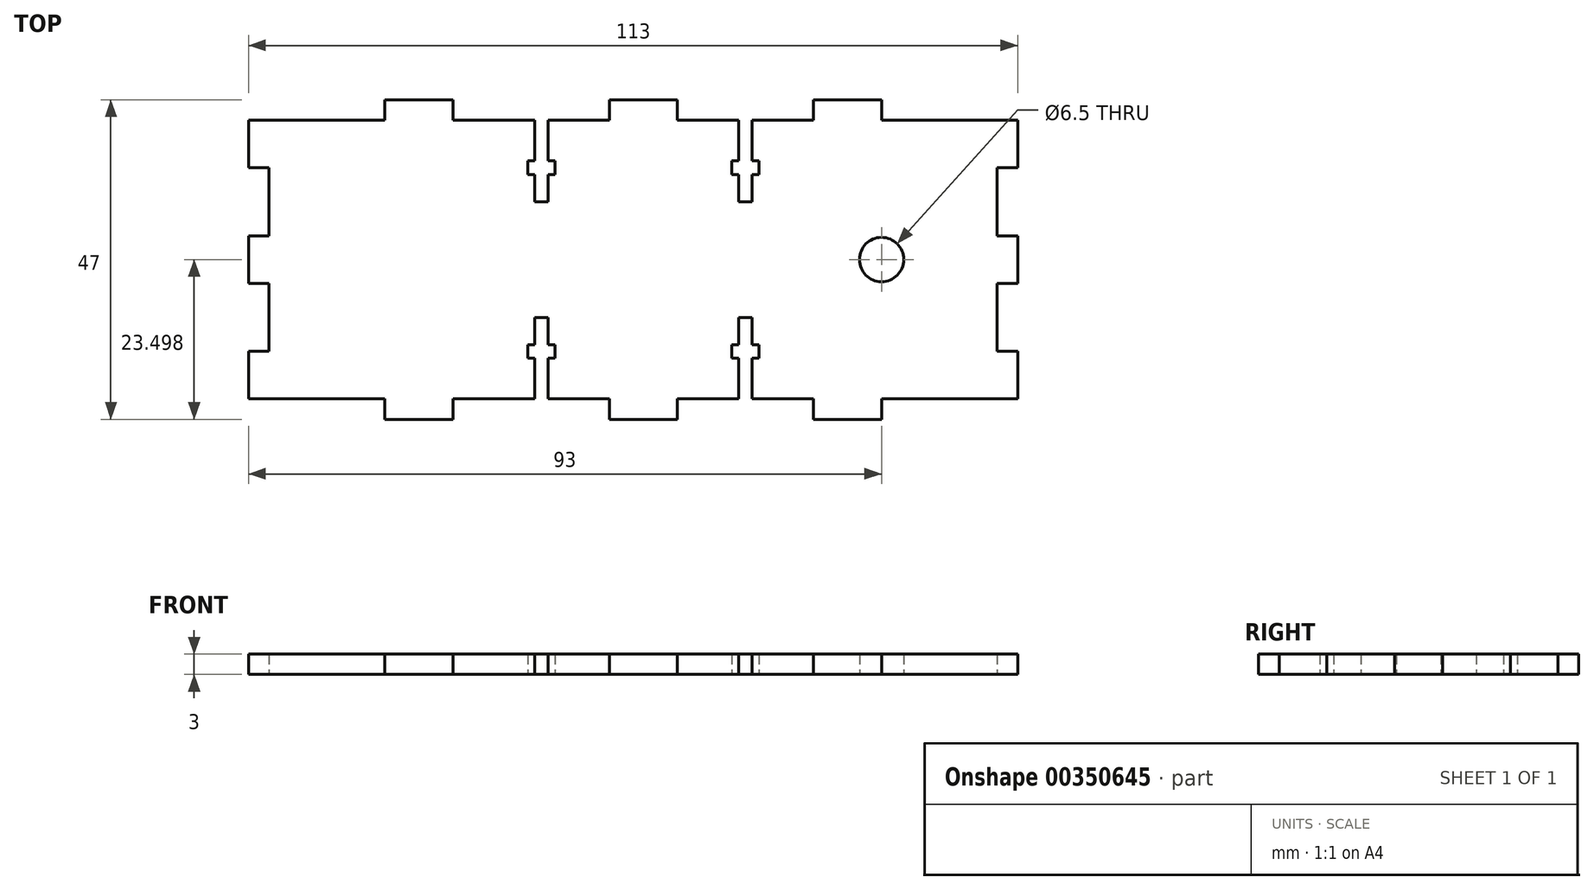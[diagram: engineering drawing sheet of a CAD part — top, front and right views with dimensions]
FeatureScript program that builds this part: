
annotation { "Feature Type Name" : "Feature", "Feature Type Description" : "" }
export const myFeature = defineFeature(function(context is Context, id is Id, definition is map)
    precondition{}
    {
        {
            var Q0;
            Q0=qCreatedBy(makeId("Top.planeOp"),FACE);
            var sketch = newSketch(context, id + "F0", { "sketchPlane" : qUnion([Q0])});
            skLineSegment(sketch, "E0", {"start": v(55.08, -54.23) * mm, "end": v(55.08, -47.23) * mm});
            skLineSegment(sketch, "E1", {"start": v(55.08, -47.23) * mm, "end": v(52.08, -47.23) * mm});
            skLineSegment(sketch, "E2", {"start": v(52.08, -47.23) * mm, "end": v(52.08, -37.23) * mm});
            skLineSegment(sketch, "E3", {"start": v(52.08, -37.23) * mm, "end": v(55.08, -37.23) * mm});
            skLineSegment(sketch, "E4", {"start": v(55.08, -37.23) * mm, "end": v(55.08, -30.23) * mm});
            skLineSegment(sketch, "E5", {"start": v(55.08, -30.23) * mm, "end": v(52.08, -30.23) * mm});
            skLineSegment(sketch, "E6", {"start": v(52.08, -30.23) * mm, "end": v(52.08, -20.23) * mm});
            skLineSegment(sketch, "E7", {"start": v(52.08, -20.23) * mm, "end": v(55.08, -20.23) * mm});
            skLineSegment(sketch, "E8", {"start": v(55.08, -20.23) * mm, "end": v(55.08, -13.23) * mm});
            skLineSegment(sketch, "E9", {"start": v(55.08, -13.23) * mm, "end": v(35.08, -13.23) * mm});
            skLineSegment(sketch, "E10", {"start": v(35.08, -13.23) * mm, "end": v(35.08, -10.23) * mm});
            skLineSegment(sketch, "E11", {"start": v(35.08, -10.23) * mm, "end": v(25.08, -10.23) * mm});
            skLineSegment(sketch, "E12", {"start": v(25.08, -10.23) * mm, "end": v(25.08, -13.23) * mm});
            skLineSegment(sketch, "E13", {"start": v(5.08, -13.23) * mm, "end": v(5.08, -10.23) * mm});
            skLineSegment(sketch, "E14", {"start": v(5.08, -10.23) * mm, "end": v(-4.92, -10.23) * mm});
            skLineSegment(sketch, "E15", {"start": v(-4.92, -10.23) * mm, "end": v(-4.92, -13.23) * mm});
            skLineSegment(sketch, "E16", {"start": v(-27.92, -13.23) * mm, "end": v(-27.92, -10.23) * mm});
            skLineSegment(sketch, "E17", {"start": v(-27.92, -10.23) * mm, "end": v(-37.92, -10.23) * mm});
            skLineSegment(sketch, "E18", {"start": v(-37.92, -10.23) * mm, "end": v(-37.92, -13.23) * mm});
            skLineSegment(sketch, "E19", {"start": v(-37.92, -13.23) * mm, "end": v(-57.92, -13.23) * mm});
            skLineSegment(sketch, "E20", {"start": v(-57.92, -13.23) * mm, "end": v(-57.92, -20.23) * mm});
            skLineSegment(sketch, "E21", {"start": v(-57.92, -20.23) * mm, "end": v(-54.92, -20.23) * mm});
            skLineSegment(sketch, "E22", {"start": v(-54.92, -20.23) * mm, "end": v(-54.92, -30.23) * mm});
            skLineSegment(sketch, "E23", {"start": v(-54.92, -30.23) * mm, "end": v(-57.92, -30.23) * mm});
            skLineSegment(sketch, "E24", {"start": v(-57.92, -30.23) * mm, "end": v(-57.92, -37.23) * mm});
            skLineSegment(sketch, "E25", {"start": v(-57.92, -37.23) * mm, "end": v(-54.92, -37.23) * mm});
            skLineSegment(sketch, "E26", {"start": v(-54.92, -37.23) * mm, "end": v(-54.92, -47.23) * mm});
            skLineSegment(sketch, "E27", {"start": v(-54.92, -47.23) * mm, "end": v(-57.92, -47.23) * mm});
            skLineSegment(sketch, "E28", {"start": v(-57.92, -54.23) * mm, "end": v(-37.92, -54.23) * mm});
            skLineSegment(sketch, "E29", {"start": v(-37.92, -54.23) * mm, "end": v(-37.92, -57.23) * mm});
            skLineSegment(sketch, "E30", {"start": v(-37.92, -57.23) * mm, "end": v(-27.92, -57.23) * mm});
            skLineSegment(sketch, "E31", {"start": v(-27.92, -57.23) * mm, "end": v(-27.92, -54.23) * mm});
            skLineSegment(sketch, "E32", {"start": v(-4.92, -54.23) * mm, "end": v(-4.92, -57.23) * mm});
            skLineSegment(sketch, "E33", {"start": v(-4.92, -57.23) * mm, "end": v(5.08, -57.23) * mm});
            skLineSegment(sketch, "E34", {"start": v(5.08, -57.23) * mm, "end": v(5.08, -54.23) * mm});
            skLineSegment(sketch, "E35", {"start": v(25.08, -54.23) * mm, "end": v(25.08, -57.23) * mm});
            skLineSegment(sketch, "E36", {"start": v(25.08, -57.23) * mm, "end": v(35.08, -57.23) * mm});
            skLineSegment(sketch, "E37", {"start": v(35.08, -57.23) * mm, "end": v(35.08, -54.23) * mm});
            skLineSegment(sketch, "E38", {"start": v(35.08, -54.23) * mm, "end": v(55.08, -54.23) * mm});
            skCircle(sketch, "E39", {"center": v(35.08, -33.73) * mm, "radius": 3.25 * mm});
            skLineSegment(sketch, "E40", {"start": v(-13.92, -54.23) * mm, "end": v(-13.92, -48.23) * mm});
            skLineSegment(sketch, "E41", {"start": v(-13.92, -48.23) * mm, "end": v(-12.92, -48.23) * mm});
            skLineSegment(sketch, "E42", {"start": v(-12.92, -48.23) * mm, "end": v(-12.92, -46.23) * mm});
            skLineSegment(sketch, "E43", {"start": v(-12.92, -46.23) * mm, "end": v(-13.92, -46.23) * mm});
            skLineSegment(sketch, "E44", {"start": v(-13.92, -46.23) * mm, "end": v(-13.92, -42.23) * mm});
            skLineSegment(sketch, "E45", {"start": v(-13.92, -42.23) * mm, "end": v(-15.92, -42.23) * mm});
            skLineSegment(sketch, "E46", {"start": v(-15.92, -42.23) * mm, "end": v(-15.92, -46.23) * mm});
            skLineSegment(sketch, "E47", {"start": v(-15.92, -46.23) * mm, "end": v(-16.92, -46.23) * mm});
            skLineSegment(sketch, "E48", {"start": v(-16.92, -46.23) * mm, "end": v(-16.92, -48.23) * mm});
            skLineSegment(sketch, "E49", {"start": v(-16.92, -48.23) * mm, "end": v(-15.92, -48.23) * mm});
            skLineSegment(sketch, "E50", {"start": v(-15.92, -48.23) * mm, "end": v(-15.92, -54.23) * mm});
            skLineSegment(sketch, "E51.MirrorCS", {"start": v(17.08, -46.23) * mm, "end": v(17.08, -48.23) * mm});
            skLineSegment(sketch, "E52.MirrorCS", {"start": v(17.08, -48.23) * mm, "end": v(16.08, -48.23) * mm});
            skLineSegment(sketch, "E53.MirrorCS", {"start": v(16.08, -46.23) * mm, "end": v(17.08, -46.23) * mm});
            skLineSegment(sketch, "E54.MirrorCS", {"start": v(14.08, -19.23) * mm, "end": v(13.08, -19.23) * mm});
            skLineSegment(sketch, "E55.MirrorCS", {"start": v(17.08, -21.23) * mm, "end": v(17.08, -19.23) * mm});
            skLineSegment(sketch, "E56.MirrorCS", {"start": v(13.08, -46.23) * mm, "end": v(14.08, -46.23) * mm});
            skLineSegment(sketch, "E57.MirrorCS", {"start": v(14.08, -48.23) * mm, "end": v(13.08, -48.23) * mm});
            skLineSegment(sketch, "E58.MirrorCS", {"start": v(16.08, -21.23) * mm, "end": v(17.08, -21.23) * mm});
            skLineSegment(sketch, "E59.MirrorCS", {"start": v(13.08, -19.23) * mm, "end": v(13.08, -21.23) * mm});
            skLineSegment(sketch, "E60.MirrorCS", {"start": v(13.08, -48.23) * mm, "end": v(13.08, -46.23) * mm});
            skLineSegment(sketch, "E61.MirrorCS", {"start": v(13.08, -21.23) * mm, "end": v(14.08, -21.23) * mm});
            skLineSegment(sketch, "E62.MirrorCS", {"start": v(17.08, -19.23) * mm, "end": v(16.08, -19.23) * mm});
            skLineSegment(sketch, "E63.MirrorCS", {"start": v(16.08, -42.23) * mm, "end": v(16.08, -46.23) * mm});
            skLineSegment(sketch, "E64.MirrorCS", {"start": v(14.08, -21.23) * mm, "end": v(14.08, -25.23) * mm});
            skLineSegment(sketch, "E65.MirrorCS", {"start": v(16.08, -25.23) * mm, "end": v(16.08, -21.23) * mm});
            skLineSegment(sketch, "E66.MirrorCS", {"start": v(14.08, -42.23) * mm, "end": v(16.08, -42.23) * mm});
            skLineSegment(sketch, "E67.MirrorCS", {"start": v(14.08, -46.23) * mm, "end": v(14.08, -42.23) * mm});
            skLineSegment(sketch, "E68.MirrorCS", {"start": v(14.08, -25.23) * mm, "end": v(16.08, -25.23) * mm});
            skLineSegment(sketch, "E69.MirrorCS", {"start": v(16.08, -48.23) * mm, "end": v(16.08, -54.23) * mm});
            skLineSegment(sketch, "E70.MirrorCS", {"start": v(14.08, -54.23) * mm, "end": v(14.08, -48.23) * mm});
            skLineSegment(sketch, "E71.MirrorCS", {"start": v(14.08, -13.23) * mm, "end": v(14.08, -19.23) * mm});
            skLineSegment(sketch, "E72.MirrorCS", {"start": v(16.08, -19.23) * mm, "end": v(16.08, -13.23) * mm});
            skLineSegment(sketch, "E73", {"start": v(-4.92, -54.23) * mm, "end": v(-13.92, -54.23) * mm});
            skLineSegment(sketch, "E74", {"start": v(-15.92, -54.23) * mm, "end": v(-27.92, -54.23) * mm});
            skLineSegment(sketch, "E75", {"start": v(14.08, -54.23) * mm, "end": v(5.08, -54.23) * mm});
            skLineSegment(sketch, "E76", {"start": v(16.08, -54.23) * mm, "end": v(25.08, -54.23) * mm});
            skLineSegment(sketch, "E77", {"start": v(25.08, -13.23) * mm, "end": v(16.08, -13.23) * mm});
            skLineSegment(sketch, "E78", {"start": v(14.08, -13.23) * mm, "end": v(5.08, -13.23) * mm});
            skLineSegment(sketch, "E79", {"start": v(-57.92, -47.23) * mm, "end": v(-57.92, -54.23) * mm});
            skLineSegment(sketch, "E80.MirrorCS", {"start": v(-16.92, -19.23) * mm, "end": v(-15.92, -19.23) * mm});
            skLineSegment(sketch, "E81.MirrorCS", {"start": v(-12.92, -21.23) * mm, "end": v(-13.92, -21.23) * mm});
            skLineSegment(sketch, "E82.MirrorCS", {"start": v(-15.92, -21.23) * mm, "end": v(-16.92, -21.23) * mm});
            skLineSegment(sketch, "E83.MirrorCS", {"start": v(-13.92, -19.23) * mm, "end": v(-12.92, -19.23) * mm});
            skLineSegment(sketch, "E84.MirrorCS", {"start": v(-15.92, -25.23) * mm, "end": v(-15.92, -21.23) * mm});
            skLineSegment(sketch, "E85.MirrorCS", {"start": v(-12.92, -19.23) * mm, "end": v(-12.92, -21.23) * mm});
            skLineSegment(sketch, "E86.MirrorCS", {"start": v(-16.92, -21.23) * mm, "end": v(-16.92, -19.23) * mm});
            skLineSegment(sketch, "E87.MirrorCS", {"start": v(-13.92, -25.23) * mm, "end": v(-15.92, -25.23) * mm});
            skLineSegment(sketch, "E88.MirrorCS", {"start": v(-13.92, -21.23) * mm, "end": v(-13.92, -25.23) * mm});
            skLineSegment(sketch, "E89.MirrorCS", {"start": v(-13.92, -13.23) * mm, "end": v(-13.92, -19.23) * mm});
            skLineSegment(sketch, "E90.MirrorCS", {"start": v(-15.92, -19.23) * mm, "end": v(-15.92, -13.23) * mm});
            skLineSegment(sketch, "E91", {"start": v(-13.92, -13.23) * mm, "end": v(-4.92, -13.23) * mm});
            skLineSegment(sketch, "E92", {"start": v(-15.92, -13.23) * mm, "end": v(-27.92, -13.23) * mm});
            skSolve(sketch);
        }
        {
            var Q0;
            Q0=makeQuery(id+"F0.imprint","IMPRINT",FACE,{"disambiguationData":[TD([[makeQuery(id+"F0.imprint","IMPRINT",EDGE,{"derivedFrom":sQuery(id+"F0.wireOp",EDGE,"E0")}),1.0]])]});
            extrude(context, id + "F1", {"entities" : qUnion([Q0]), "depth" : 3 * mm});
        }
    });
